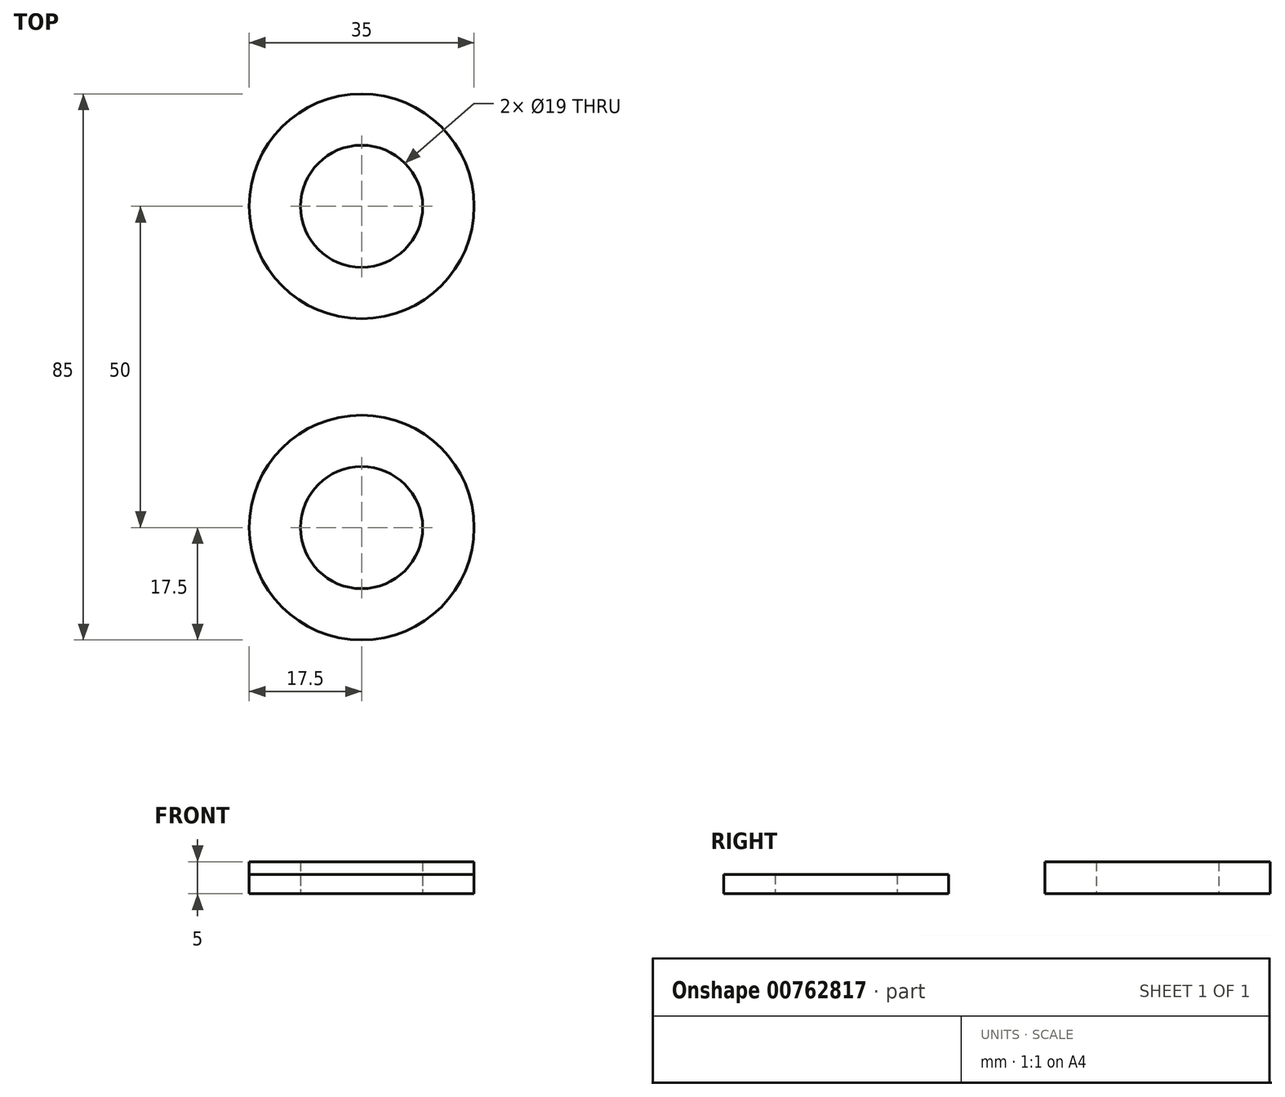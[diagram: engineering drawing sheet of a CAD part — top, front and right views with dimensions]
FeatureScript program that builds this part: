
annotation { "Feature Type Name" : "Feature", "Feature Type Description" : "" }
export const myFeature = defineFeature(function(context is Context, id is Id, definition is map)
    precondition{}
    {
        {
            var Q0;
            Q0=qCreatedBy(makeId("Top.planeOp"),FACE);
            var sketch = newSketch(context, id + "F0", { "sketchPlane" : qUnion([Q0])});
            skCircle(sketch, "E0", {"center": v(0, 0) * mm, "radius": 17.5 * mm});
            skCircle(sketch, "E1", {"center": v(0, 0) * mm, "radius": 9.5 * mm});
            skSolve(sketch);
        }
        {
            var Q0;
            Q0=makeQuery(id+"F0.imprint","IMPRINT",FACE,{"disambiguationData":[TD([[makeQuery(id+"F0.imprint","IMPRINT",EDGE,{"derivedFrom":sQuery(id+"F0.wireOp",EDGE,"E0")}),1.0]])]});
            extrude(context, id + "F1", {"entities" : qUnion([Q0]), "depth" : 3 * mm, "offsetDistance" : 25 * mm});
        }
        {
            var Q0;
            Q0=makeQuery(id+"F1.opExtrude","SWEPT_BODY",BODY,{"disambiguationData":[OSD([sQuery(id+"F0.wireOp",EDGE,"E0"),sQuery(id+"F0.wireOp",EDGE,"E1")])]});
            transform(context, id + "F2", {"entities" : qUnion([Q0]), "transformType" : TransformType.TRANSLATION_3D, "dx" : 0 * mm, "dy" : 50 * mm, "dz" : 0 * mm, "makeCopy" : true});
        }
        {
            var Q0;
            Q0=makeQuery(id+"F2.opPattern","COPY",FACE,{"derivedFrom":makeQuery(id+"F1.opExtrude","CAP_FACE",FACE,{"disambiguationData":[OSD([sQuery(id+"F0.wireOp",EDGE,"E0"),sQuery(id+"F0.wireOp",EDGE,"E1")])],"isStart":false}),"instanceName":"1"});
            extrude(context, id + "F3", {"entities" : qUnion([Q0]), "operationType" : NewBodyOperationType.ADD, "depth" : 2 * mm, "offsetDistance" : 25 * mm});
        }
    });
